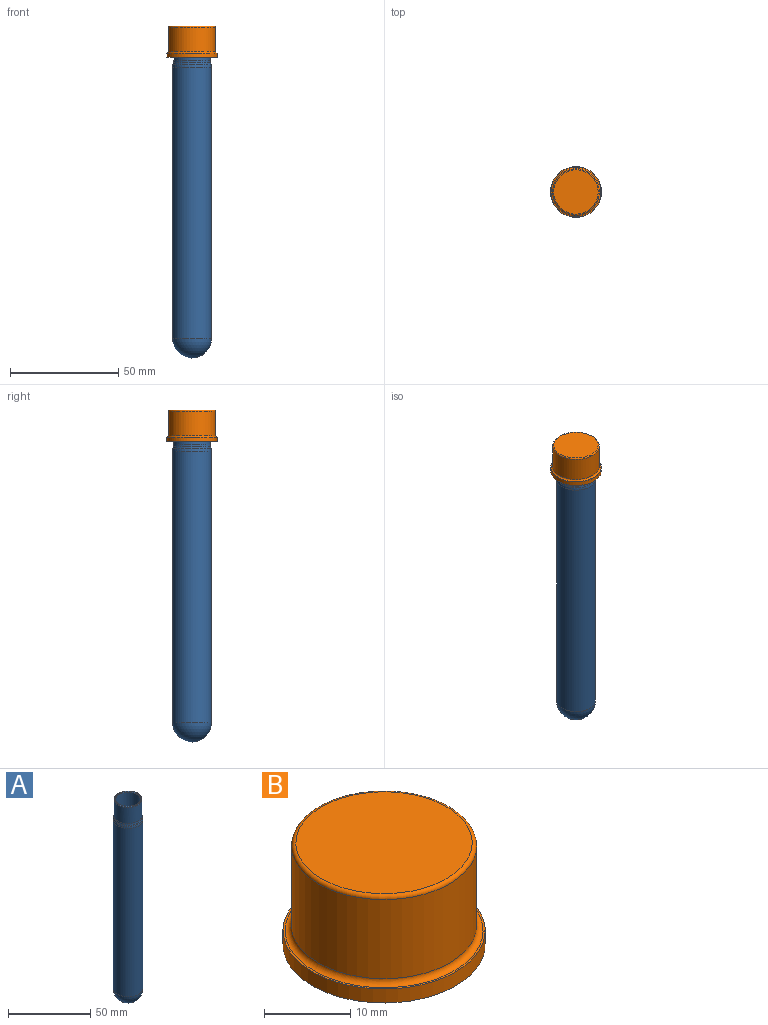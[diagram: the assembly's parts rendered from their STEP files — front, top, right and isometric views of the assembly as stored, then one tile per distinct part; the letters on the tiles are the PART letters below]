
ASSEMBLY  parts=2 mates=1
PART A: 15 faces, bbox 21.5x21.5x150 mm
  f0: cylinder r=8.5mm len=17mm, axis (0,0,1), area 642.7mm2, adj f1,f14
  f1: torus R=13.5mm, axis (0,0,1), area 65.8mm2, adj f0,f2
  f2: cone r=8.65mm half-angle=14deg, axis (0,0,-1), area 45.7mm2, adj f1,f3
  f3: torus R=4mm, axis (0,0,1), area 68.9mm2, adj f2,f4
  f4: cylinder r=9mm len=125.38mm, axis (0,0,1), area 7090.3mm2, adj f3,f5
  f5: sphere r=9mm, area 508.9mm2, adj f4
  f6: plane 16.3x16.3mm, normal (0,0,1), area 15.1mm2, adj f13,f14
  f7: cylinder r=7.5mm len=15mm, axis (0,0,1), area 567.1mm2, adj f8,f13
  f8: torus R=13.5mm, axis (0,0,1), area 69.8mm2, adj f7,f9
  f9: cone r=7.68mm half-angle=14deg, axis (0,0,-1), area 40.6mm2, adj f8,f10
  f10: torus R=4mm, axis (0,0,1), area 49mm2, adj f9,f11
  f11: cylinder r=8mm len=125.38mm, axis (0,0,1), area 6302.5mm2, adj f10,f12
  f12: sphere r=8mm, area 402.1mm2, adj f11
  f13: torus R=7.85mm, axis (0,0,-1), area 26.3mm2, adj f6,f7
  f14: torus R=8.15mm, axis (0,0,-1), area 28.9mm2, adj f0,f6
PART B: 10 faces, bbox 24.9x24.9x14.5 mm
  f0: plane 20.5x20.5mm, normal (0,0,1), area 330.1mm2, adj f7
  f1: cylinder r=10.75mm len=21.5mm, axis (0,0,1), area 759.9mm2, adj f7,f9
  f2: plane 23.5x23.5mm, normal (0,0,1), area 18.3mm2, adj f3,f9
  f3: cylinder r=11.75mm len=23.5mm, axis (0,0,1), area 147.7mm2, adj f2,f4
  f4: plane 23.5x23.5mm, normal (0,0,-1), area 135.1mm2, adj f3,f8
  f5: cylinder r=9.25mm len=18.5mm, axis (0,0,1), area 610.3mm2, adj f6,f8
  f6: plane 18.5x18.5mm, normal (0,0,-1), area 268.8mm2, adj f5
  f7: torus R=10.25mm, axis (0,0,-1), area 52.2mm2, adj f0,f1
  f8: torus R=9.75mm, axis (0,0,1), area 46.5mm2, adj f4,f5
  f9: torus R=11.5mm, axis (0,0,-1), area 81.6mm2, adj f1,f2
PLACE A t=(-51.5,6.64,-20.44)mm
PLACE B t=(-51.5,6.64,118.56)mm
MATE revolute B.f1 <-> A.f0  axis (0,0,-1) through (-51.5,6.64,129.56)mm
